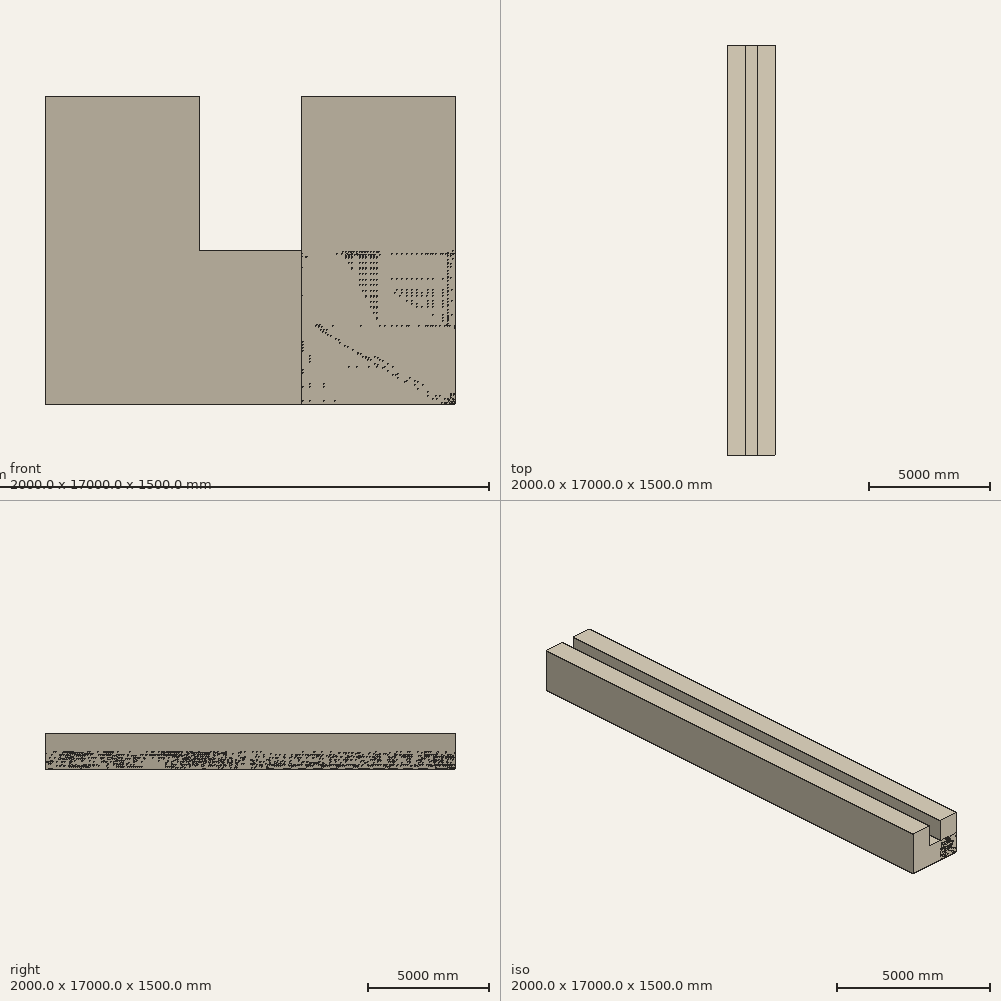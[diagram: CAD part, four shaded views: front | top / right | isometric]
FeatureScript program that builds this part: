
annotation { "Feature Type Name" : "Feature", "Feature Type Description" : "" }
export const myFeature = defineFeature(function(context is Context, id is Id, definition is map)
    precondition{}
    {
        {
            var Q0;
            Q0=qCreatedBy(makeId("Top.planeOp"),FACE);
            var sketch = newSketch(context, id + "F0", { "sketchPlane" : qUnion([Q0])});
            skLineSegment(sketch, "E0.bottom", {"start": v(1000, 8500) * mm, "end": v(-1000, 8500) * mm});
            skLineSegment(sketch, "E0.top", {"start": v(1000, -8500) * mm, "end": v(-1000, -8500) * mm});
            skLineSegment(sketch, "E0.left", {"start": v(1000, 8500) * mm, "end": v(1000, -8500) * mm});
            skLineSegment(sketch, "E0.right", {"start": v(-1000, 8500) * mm, "end": v(-1000, -8500) * mm});
            skPoint(sketch, "E0.middle", {"position": v(0, 0) * mm});
            skLineSegment(sketch, "E1", {"start": v(-1000, -8500) * mm, "end": v(-250, -8500) * mm});
            skLineSegment(sketch, "E2", {"start": v(-250, -8500) * mm, "end": v(250, -8500) * mm});
            skLineSegment(sketch, "E3", {"start": v(250, -8500) * mm, "end": v(1000, -8500) * mm});
            skLineSegment(sketch, "E4", {"start": v(-250, -8500) * mm, "end": v(-250, 8500) * mm});
            skLineSegment(sketch, "E5", {"start": v(-250, 8500) * mm, "end": v(-1000, 8500) * mm});
            skLineSegment(sketch, "E6", {"start": v(250, -8500) * mm, "end": v(250, 8500) * mm});
            skLineSegment(sketch, "E7", {"start": v(250, 8500) * mm, "end": v(1000, 8500) * mm});
            skLineSegment(sketch, "E8", {"start": v(1000, -8500) * mm, "end": v(250, -8500) * mm});
            skSolve(sketch);
        }
        {
            var Q0;
            Q0=makeQuery(id+"F0.imprint","IMPRINT",FACE,{"disambiguationData":[TD([[makeQuery(id+"F0.imprint","IMPRINT",EDGE,{"derivedFrom":sQuery(id+"F0.wireOp",EDGE,"E0.bottom")}),1.0]])]});
            extrude(context, id + "F1", {"entities" : qUnion([Q0]), "depth" : 750 * mm});
        }
        {
            var Q0;
            Q0=makeQuery(id+"F0.imprint","IMPRINT",FACE,{"disambiguationData":[TD([[makeQuery(id+"F0.imprint","IMPRINT",EDGE,{"derivedFrom":sQuery(id+"F0.wireOp",EDGE,"E0.left")}),-1.0]])]});
            extrude(context, id + "F2", {"entities" : qUnion([Q0]), "depth" : 1500 * mm});
        }
        {
            var Q0;
            Q0=makeQuery(id+"F0.imprint","IMPRINT",FACE,{"disambiguationData":[TD([[makeQuery(id+"F0.imprint","IMPRINT",EDGE,{"derivedFrom":sQuery(id+"F0.wireOp",EDGE,"E0.right")}),1.0]])]});
            extrude(context, id + "F3", {"entities" : qUnion([Q0]), "operationType" : NewBodyOperationType.ADD, "depth" : 1500 * mm});
        }
    });
